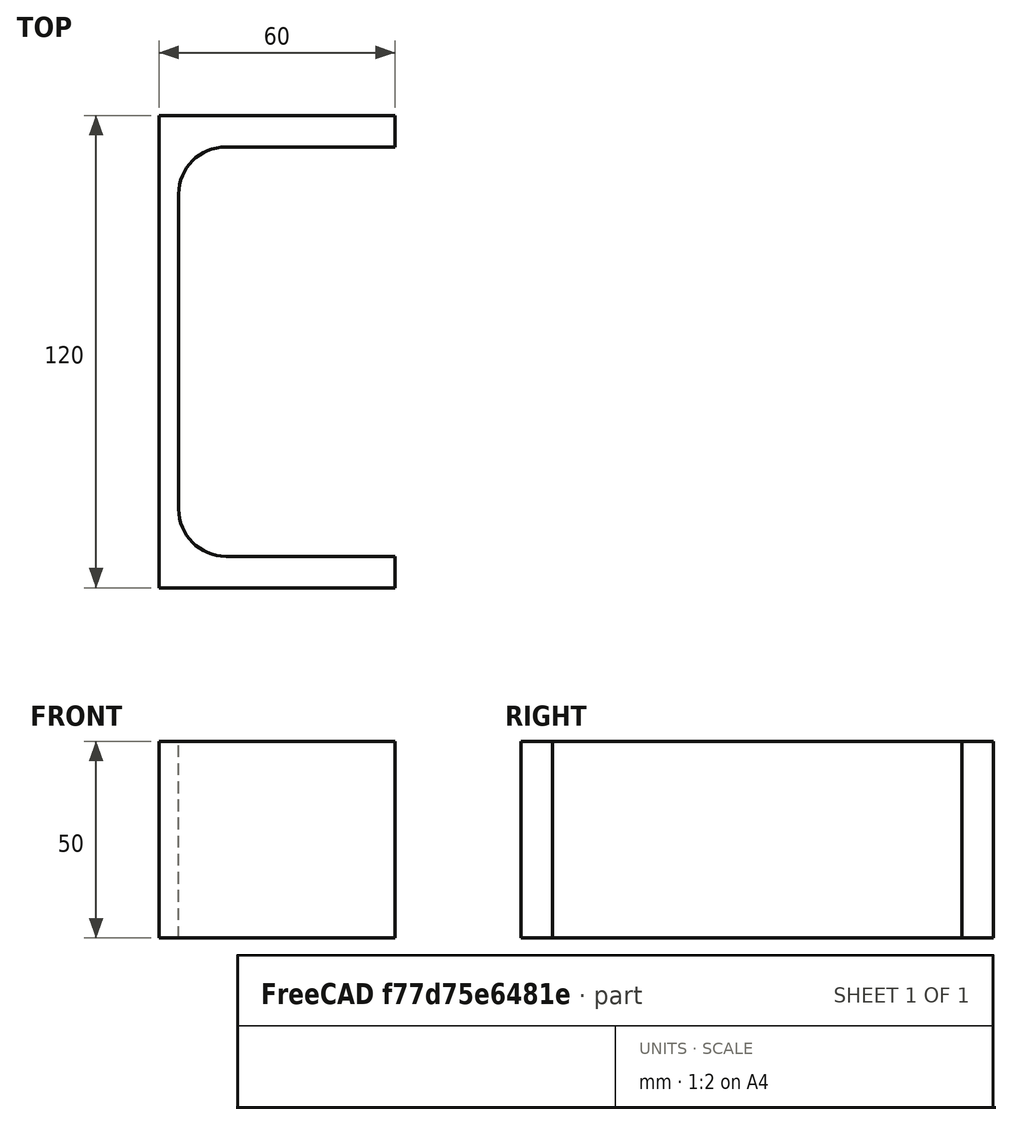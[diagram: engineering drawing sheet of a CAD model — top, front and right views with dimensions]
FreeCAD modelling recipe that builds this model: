
FCSTD DOCUMENT  (FreeCAD 0.20R29410 (Git))
Label: UPE-Profile 120 DIN1026-2 S235JR
License: All rights reserved
LicenseURL: http://en.wikipedia.org/wiki/All_rights_reserved
objects: Sketcher::SketchObject×1, Part::Extrusion×1
note: 2 computed .brp shape members not serialized (recipe doc carries the construction recipe); baked Part::Feature solids carry a one-line shape summary decoded from their .brp

FEATURE [Sketcher::SketchObject] Sketch
  FullyConstrained = true
  MapMode = 5
  sketch-geometry (10):
    g0: LineSegment StartX=5 StartY=-40 StartZ=0 EndX=5 EndY=40 EndZ=0
    g1: LineSegment StartX=17 StartY=52 StartZ=0 EndX=60 EndY=52 EndZ=0
    g2: LineSegment StartX=60 StartY=52 StartZ=0 EndX=60 EndY=60 EndZ=0
    g3: LineSegment StartX=60 StartY=-60 StartZ=0 EndX=60 EndY=-52 EndZ=0
    g4: LineSegment StartX=60 StartY=-52 StartZ=0 EndX=17 EndY=-52 EndZ=0
    g5: ArcOfCircle CenterX=17 CenterY=40 CenterZ=0 NormalX=0 NormalY=0 NormalZ=1 AngleXU=0 Radius=12 StartAngle=1.5708 EndAngle=3.14159
    g6: ArcOfCircle CenterX=17 CenterY=-40 CenterZ=0 NormalX=0 NormalY=0 NormalZ=1 AngleXU=0 Radius=12 StartAngle=3.14159 EndAngle=4.71239
    g7: LineSegment StartX=60 StartY=-60 StartZ=0 EndX=0 EndY=-60 EndZ=0
    g8: LineSegment StartX=0 StartY=-60 StartZ=0 EndX=0 EndY=60 EndZ=0
    g9: LineSegment StartX=0 StartY=60 StartZ=0 EndX=60 EndY=60 EndZ=0
  constraints (27):
    c: Vertical(g0)
    c: Coincident(g2,g1)
    c: Vertical(g2)
    c: Vertical(g3)
    c: Coincident(g4,g3)
    c: Horizontal(g4)
    c: Tangent(g1,g5) = 1.5708
    c: Tangent(g0,g5) = 1.5708
    c: Tangent(g0,g6) = 1.5708
    c: Tangent(g4,g6) = 1.5708
    c: Symmetric(g2,g3,g-1)
    c: DistanceY(g2) = 8
    c: Radius(g5) = 12
    c: Coincident(g3,g7)
    c: PointOnObject(g7,g-2)
    c: Horizontal(g7)
    c: Coincident(g7,g8)
    c: PointOnObject(g8,g-2)
    c: Coincident(g8,g9)
    c: Coincident(g9,g2)
    c: Horizontal(g9)
    c: Distance(g-1,g0) = 5
    c: DistanceX(g9,g9) = 60
    c: Horizontal(g1)
    c: Equal(g3,g2)
    c: Equal(g5,g6)
    c: DistanceY(g3,g2) = 120
FEATURE [Part::Extrusion] Extrude  label="UPE-Profile 120 DIN1026-2 S235JR"
  Base = -> Sketch
  Dir = (0,0,50)
  DirMode = 0
  FaceMakerClass = Part::FaceMakerExtrusion
  LengthFwd = 0
  LengthRev = 0
  Solid = true
  Symmetric = false
